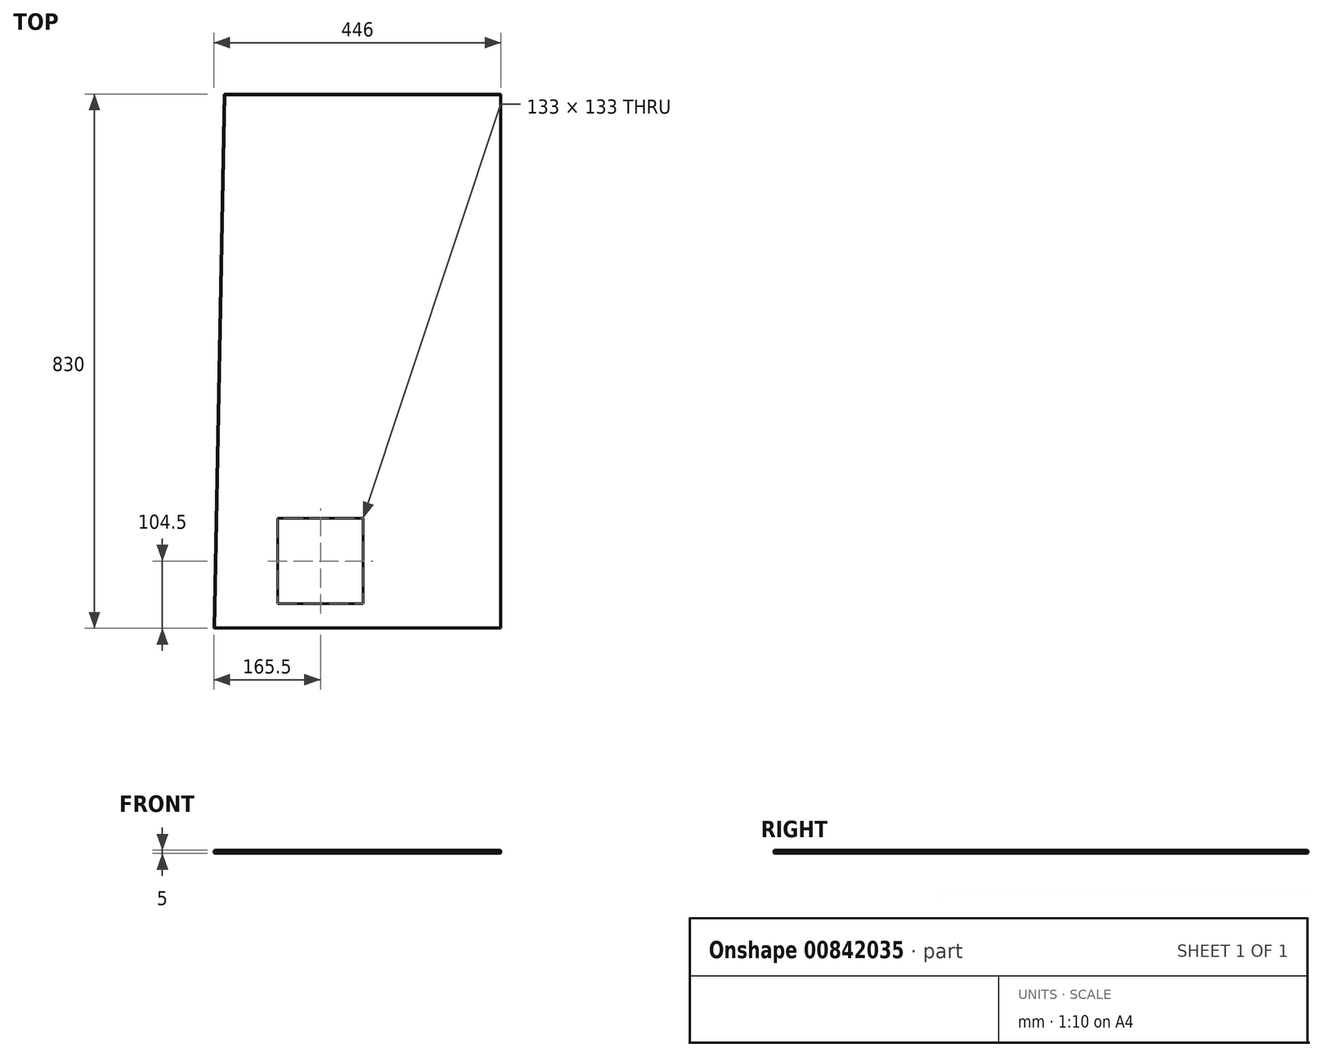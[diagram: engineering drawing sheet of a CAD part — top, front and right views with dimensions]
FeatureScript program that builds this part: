
annotation { "Feature Type Name" : "Feature", "Feature Type Description" : "" }
export const myFeature = defineFeature(function(context is Context, id is Id, definition is map)
    precondition{}
    {
        {
            var Q0;
            Q0=qCreatedBy(makeId("Top.planeOp"),FACE);
            var sketch = newSketch(context, id + "F0", { "sketchPlane" : qUnion([Q0])});
            skLineSegment(sketch, "E0.top", {"start": v(-223, -415) * mm, "end": v(223, -415) * mm});
            skLineSegment(sketch, "E0.right", {"start": v(223, 415) * mm, "end": v(223, -415) * mm});
            skPoint(sketch, "E0.middle", {"position": v(0, 0) * mm});
            skLineSegment(sketch, "E1", {"start": v(223, 415) * mm, "end": v(-207, 415) * mm});
            skLineSegment(sketch, "E2", {"start": v(-207, 415) * mm, "end": v(-223, -415) * mm});
            skSolve(sketch);
        }
        {
            var Q0;
            Q0=makeQuery(id+"F0.imprint","IMPRINT",FACE,{"disambiguationData":[TD([[makeQuery(id+"F0.imprint","IMPRINT",EDGE,{"derivedFrom":sQuery(id+"F0.wireOp",EDGE,"E0.top")}),1.0]])]});
            extrude(context, id + "F1", {"entities" : qUnion([Q0]), "endBound" : BoundingType.SYMMETRIC, "depth" : 5 * mm, "offsetDistance" : 25 * mm});
        }
        {
            var Q0;
            Q0=makeQuery(id+"F1.opExtrude","CAP_FACE",FACE,{"disambiguationData":[OSD([sQuery(id+"F0.wireOp",EDGE,"E0.bottom"),sQuery(id+"F0.wireOp",EDGE,"E0.top"),sQuery(id+"F0.wireOp",EDGE,"E0.left"),sQuery(id+"F0.wireOp",EDGE,"E0.right")])],"isStart":false});
            var sketch = newSketch(context, id + "F2", { "sketchPlane" : qUnion([Q0])});
            skLineSegment(sketch, "E3.bottom", {"start": v(-124, -244) * mm, "end": v(9, -244) * mm});
            skLineSegment(sketch, "E3.top", {"start": v(-124, -377) * mm, "end": v(9, -377) * mm});
            skLineSegment(sketch, "E3.left", {"start": v(-124, -244) * mm, "end": v(-124, -377) * mm});
            skLineSegment(sketch, "E3.right", {"start": v(9, -244) * mm, "end": v(9, -377) * mm});
            skSolve(sketch);
        }
        {
            var Q0;
            Q0=makeQuery(id+"F2.imprint","IMPRINT",FACE,{"disambiguationData":[TD([[makeQuery(id+"F2.imprint","IMPRINT",EDGE,{"derivedFrom":sQuery(id+"F2.wireOp",EDGE,"E3.bottom")}),-1.0]])]});
            extrude(context, id + "F3", {"entities" : qUnion([Q0]), "operationType" : NewBodyOperationType.REMOVE, "endBound" : BoundingType.THROUGH_ALL, "oppositeDirection" : true, "depth" : 25 * mm, "offsetDistance" : 25 * mm});
        }
        {
            var Q0;
            Q0=makeQuery(id+"F1.opExtrude","CAP_EDGE",EDGE,{"disambiguationData":[OSD([sQuery(id+"F0.wireOp",EDGE,"E2")])],"isStart":false});
            var Q1;
            Q1=makeQuery(id+"F1.opExtrude","CAP_EDGE",EDGE,{"disambiguationData":[OSD([sQuery(id+"F0.wireOp",EDGE,"E2")])],"isStart":true});
            var Q2;
            Q2=makeQuery(id+"F1.opExtrude","CAP_EDGE",EDGE,{"disambiguationData":[OSD([sQuery(id+"F0.wireOp",EDGE,"E1")])],"isStart":false});
            var Q3;
            Q3=makeQuery(id+"F1.opExtrude","CAP_EDGE",EDGE,{"disambiguationData":[OSD([sQuery(id+"F0.wireOp",EDGE,"E1")])],"isStart":true});
            var Q4;
            Q4=makeQuery(id+"F1.opExtrude","CAP_EDGE",EDGE,{"disambiguationData":[OSD([sQuery(id+"F0.wireOp",EDGE,"E0.right")])],"isStart":false});
            var Q5;
            Q5=makeQuery(id+"F1.opExtrude","CAP_EDGE",EDGE,{"disambiguationData":[OSD([sQuery(id+"F0.wireOp",EDGE,"E0.right")])],"isStart":true});
            var Q6;
            Q6=makeQuery(id+"F1.opExtrude","CAP_EDGE",EDGE,{"disambiguationData":[OSD([sQuery(id+"F0.wireOp",EDGE,"E0.top")])],"isStart":false});
            var Q7;
            Q7=makeQuery(id+"F1.opExtrude","CAP_EDGE",EDGE,{"disambiguationData":[OSD([sQuery(id+"F0.wireOp",EDGE,"E0.top")])],"isStart":true});
            chamfer(context, id + "F4", {"entities" : qUnion([Q0, Q1, Q2, Q3, Q4, Q5, Q6, Q7]), "width" : 1 * mm, "tangentPropagation" : true});
        }
    });
